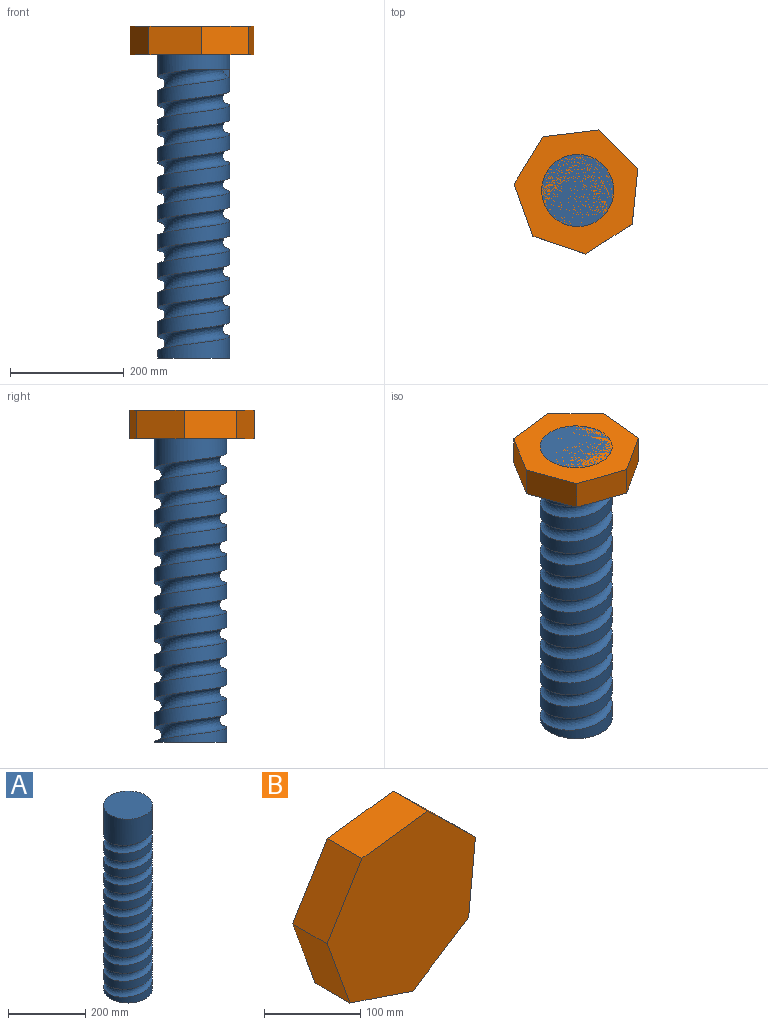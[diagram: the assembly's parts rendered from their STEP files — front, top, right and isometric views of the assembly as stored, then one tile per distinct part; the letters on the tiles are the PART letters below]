
ASSEMBLY  parts=2 mates=1
PART A: 17 faces, bbox 190.3x190.3x609.4 mm
  f0: cylinder r=63.5mm len=127mm, axis (0,0,-1), area 5700.5mm2, adj f1,f11,f13,f14
  f1: cylinder r=63.5mm len=127mm, axis (0,0,-1), area 10134.6mm2, adj f0,f2,f14
  f2: cylinder r=63.5mm len=127mm, axis (0,0,-1), area 10134.4mm2, adj f1,f3,f14
  f3: cylinder r=63.5mm len=127mm, axis (0,0,-1), area 10134.1mm2, adj f2,f4,f14
  f4: cylinder r=63.5mm len=127mm, axis (0,0,-1), area 10133.9mm2, adj f3,f5,f14
  f5: cylinder r=63.5mm len=127mm, axis (0,0,-1), area 10133.8mm2, adj f4,f6,f14
  f6: cylinder r=63.5mm len=127mm, axis (0,0,-1), area 10133.8mm2, adj f5,f7,f14
  f7: cylinder r=63.5mm len=127mm, axis (0,0,-1), area 10133.9mm2, adj f6,f8,f14
  f8: cylinder r=63.5mm len=127mm, axis (0,0,-1), area 10134.1mm2, adj f7,f9,f14
  f9: cylinder r=63.5mm len=127mm, axis (0,0,-1), area 10134.4mm2, adj f8,f10,f14
  f10: cylinder r=63.5mm len=127mm, axis (0,0,-1), area 36103.4mm2, adj f9,f12,f14,f15,f16
  f11: plane 139.48x139.47mm, normal (0,0,-1), area 11757.5mm2, adj f0,f13,f14
  f12: plane 16.3x16.3mm, normal (0,-1,0), area 126.7mm2, adj f10,f14,f16
  f13: plane 16.3x16.3mm, normal (0,1,0), area 126.7mm2, adj f0,f11,f14
  f14: bspline ~533.4x177.8mm, area 138019.6mm2, adj f0,f1,f2,f3,f4,f5,f6,f7
  f15: plane 127x127mm, normal (0,0,1), area 12667.7mm2, adj f10
  f16: plane 75.98x75.97mm, normal (0,0,-1), area 910.3mm2, adj f10,f12,f14
PART B: 9 faces, bbox 217.9x50.8x218.4 mm
  f0: plane 92.54x50.8mm, normal (-0.32,0,-0.95), area 4962.6mm2, adj f1,f6,f7,f8
  f1: plane 82.17x52.83mm, normal (0.54,0,-0.84), area 4962.6mm2, adj f0,f2,f7,f8
  f2: plane 97.18x50.8mm, normal (0.99,0,-0.1), area 4962.6mm2, adj f1,f3,f7,f8
  f3: plane 69.79x68.35mm, normal (0.7,0,0.71), area 4962.6mm2, adj f2,f4,f7,f8
  f4: plane 96.96x50.8mm, normal (-0.12,0,0.99), area 4962.6mm2, adj f3,f5,f7,f8
  f5: plane 83.25x51.11mm, normal (-0.85,0,0.52), area 4962.6mm2, adj f4,f6,f7,f8
  f6: plane 91.87x50.8mm, normal (-0.94,0,-0.34), area 4962.6mm2, adj f0,f5,f7,f8
  f7: plane 218.37x217.86mm, normal (0,-1,0), area 34678.9mm2, adj f0,f1,f2,f3,f4,f5,f6
  f8: plane 218.37x217.86mm, normal (0,1,0), area 34678.9mm2, adj f0,f1,f2,f3,f4,f5,f6
PLACE A at identity
PLACE B rot(axis=(-1,0,0),90deg) t=(710.82,-343.23,533.4)mm
MATE cylindrical B.f7 <-> A.f0  axis (0,0,1) through (0,0,584.2)mm
